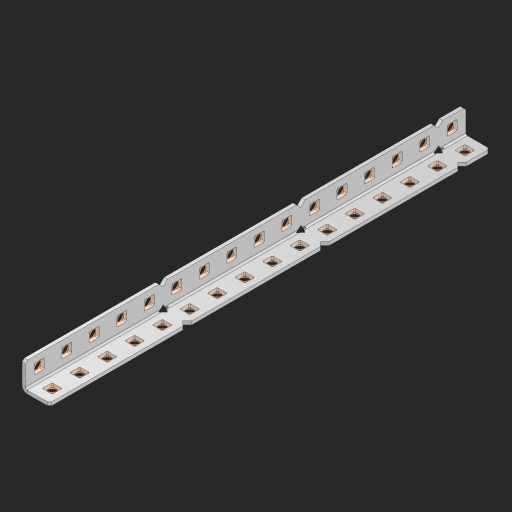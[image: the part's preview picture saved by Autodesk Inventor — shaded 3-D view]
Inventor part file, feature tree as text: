
AUTODESK INVENTOR PART (.ipt)
format: ipt  version: 2023 (Build 270158000, 158)  size: 736,768 bytes
history: native  units: in
note: dims shown in document units (in); Inventor stores cm internally (conversion verified against a paired STEP export)
features: other x38, extrude x33, sheet_metal_op x8, sketch x5, pattern_linear x1, mirror x1, chamfer x1
ambient origin geometry x8: Origin, YZ Plane, XZ Plane, XY Plane, X Axis, Y Axis, Z Axis, Center Point
bodies: Solid1 (feature_tree), Body (feature_tree)
feature tree (87):
  sheet_metal_op  "Flanges"
  sheet_metal_op  "Body Pattern"
  other  "Arc Length"
  pattern_linear  "Notch Pattern"  Spacing1=0.125in  [1 undecoded]
  other  "Diagonal Plane"
  mirror  "Everything Mirrored"
  chamfer  "End Chamfer"
  sketch  "Sketch1"  dims[d0=0.5in]
  other  "Plate1"
  sketch  "Sketch2"  dims[d1=8.0in]
  other  "Plate2"
  sheet_metal_op  "Bend1"
  sheet_metal_op  "Corner1"
  sketch  "Sketch8"  dims[d2=0.0625in]
  sketch  "Sketch9"  dims[d3=0.0625in]
  other  "Srf91"
  sheet_metal_op  "Body Pattern Sketch"
  other  "Srf92"
  sketch  "Sketch13"  dims[d4=0.0312in d5=0.125in d6=0.0625in d7=0.5in d8=90.0deg d9=0.0312in d10=0.25in d11=0.0625in d12=0.0625in d49=0.182in d50=0.02in d52=0.25in d53=0.0625in d54=0.0in d55=0.172in d56=1.0in d57=0.0in d85=0.1473in d86=0.1782in d89=0.0625in d90=0.0in d91=0.04in d92=0.0491in d95=2.5in d96=0.04in d97=0.25in d98=45.0deg d123=0.204in d126=0.0491in d127=0.1473in d128=0.08in d129=0.04in d130=2.5in d131=6.2992in d133=0.5in d134=0.3937in d136=1.0in]
  other  "Srf856"
  other  "Srf857"
  other  "Srf858"
  other  "Srf859"
  other  "Srf860"
  other  "Srf861"
  other  "Srf1275"
  other  "Srf1276"
  other  "Srf1278"
  other  "Srf1279"
  other  "Srf1280"
  other  "Srf1281"
  other  "Srf1282"
  other  "Srf1283"
  other  "Srf1383"
  other  "Srf1384"
  other  "Srf1385"
  other  "Srf1386"
  other  "Srf1387"
  other  "Srf1388"
  other  "Srf1389"
  other  "Srf1390"
  other  "Srf1391"
  other  "Srf1475"
  other  "Srf1476"
  other  "Srf1477"
  other  "Srf1478"
  other  "Srf1479"
  other  "Srf1480"
  other  "Srf1481"
  other  "Srf1482"
  other  "Srf1483"
  sheet_metal_op  "Body Stamp"
  sheet_metal_op  "Body Circle"
  sheet_metal_op  "Notch"
  extrude  "ExtrusionSrf92"  Depth=0.0625in
  extrude  "ExtrusionSrf856"  Depth=0.5in TaperAngle=90.0deg
  extrude  "ExtrusionSrf857"  Depth=0.25in
  extrude  "ExtrusionSrf858"  Depth=0.0625in
  extrude  "ExtrusionSrf859"  Depth=0.0625in
  extrude  "ExtrusionSrf860"  Depth=0.3937in
  extrude  "ExtrusionSrf861"  Depth=0.02in
  extrude  "ExtrusionSrf1275"  Depth=0.25in
  extrude  "ExtrusionSrf1276"  Depth=0.0625in
  extrude  "ExtrusionSrf1277"  TaperAngle=0.0deg  [1 undecoded]
  extrude  "ExtrusionSrf1278"  Depth=0.3937in
  extrude  "ExtrusionSrf1279"  Depth=0.3937in TaperAngle=0.0deg
  extrude  "ExtrusionSrf1280"  Depth=0.3937in
  extrude  "ExtrusionSrf1281"  Depth=0.3937in
  extrude  "ExtrusionSrf1282"  Depth=0.0625in
  extrude  "ExtrusionSrf1383"  Depth=0.3937in TaperAngle=0.0deg
  extrude  "ExtrusionSrf1384"  Depth=0.3937in
  extrude  "ExtrusionSrf1385"  Depth=0.25in TaperAngle=45.0deg
  extrude  "ExtrusionSrf1386"  Depth=0.3937in
  extrude  "ExtrusionSrf1387"  Depth=0.3937in
  extrude  "ExtrusionSrf1388"  Depth=0.3937in
  extrude  "ExtrusionSrf1389"  Depth=0.3937in
  extrude  "ExtrusionSrf1390"  Depth=0.3937in
  extrude  "ExtrusionSrf1391"  Depth=0.3937in
  extrude  "ExtrusionSrf1475"  Depth=0.3937in
  extrude  "ExtrusionSrf1476"  Depth=0.5in
  extrude  "ExtrusionSrf1477"  [1 undecoded]
  extrude  "ExtrusionSrf1478"  [1 undecoded]
  extrude  "ExtrusionSrf1479"  [1 undecoded]
  extrude  "ExtrusionSrf1480"  [1 undecoded]
  extrude  "ExtrusionSrf1481"  [1 undecoded]
  extrude  "ExtrusionSrf1482"  [1 undecoded]
  extrude  "ExtrusionSrf1483"  [1 undecoded]
note: 9 required parameter values undecoded (feature->parameter linkage not recoverable at this tier; creation-order binding heuristic only, values carry confidence <= 0.55)
